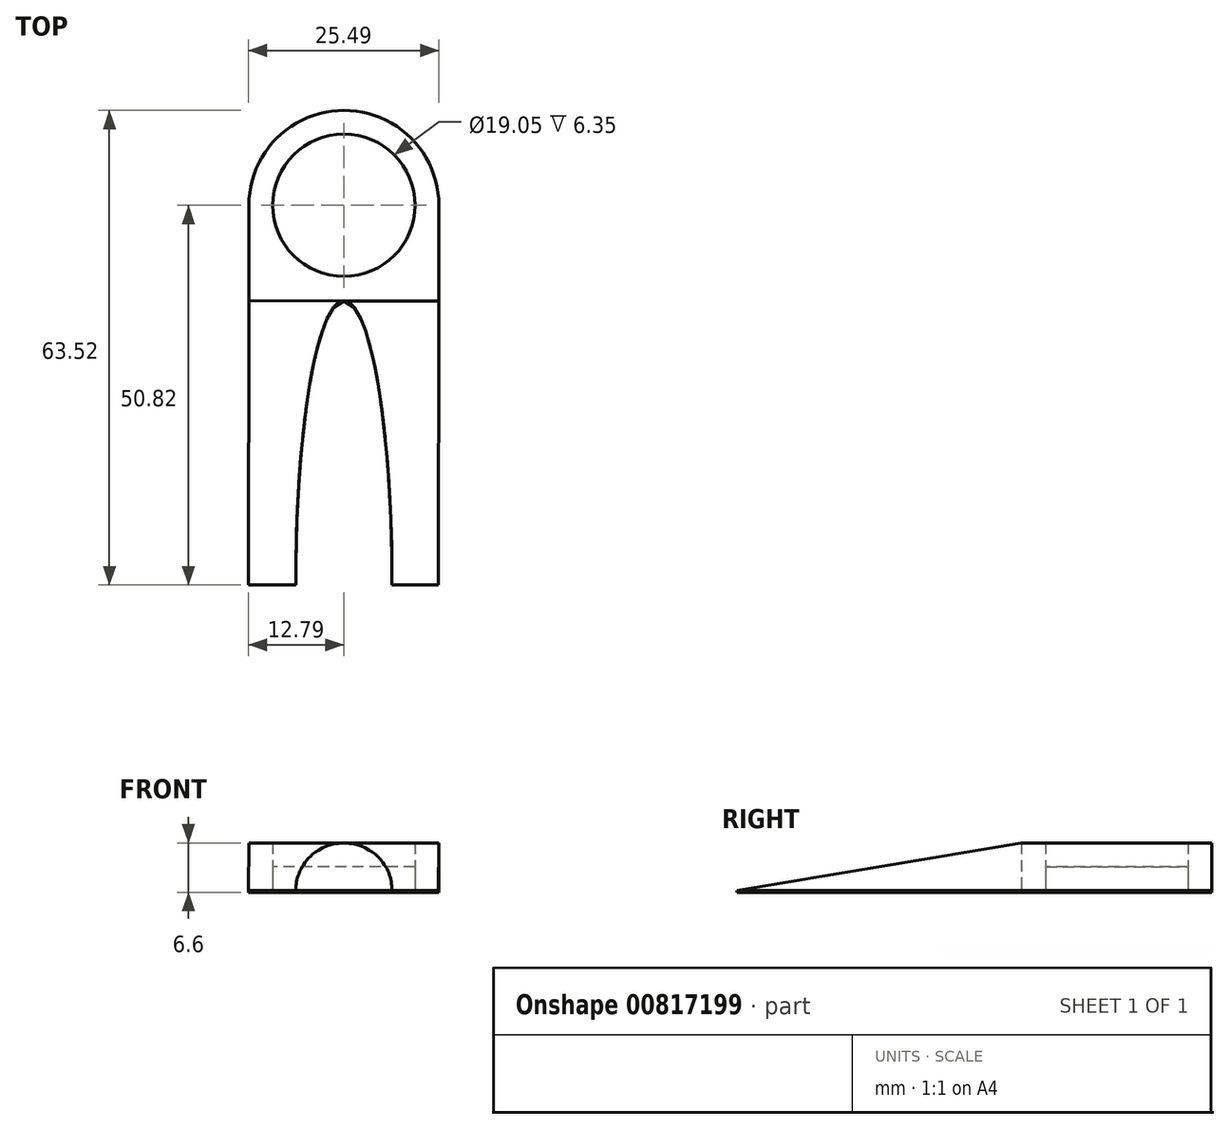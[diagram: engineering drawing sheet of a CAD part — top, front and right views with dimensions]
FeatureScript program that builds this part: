
annotation { "Feature Type Name" : "Feature", "Feature Type Description" : "" }
export const myFeature = defineFeature(function(context is Context, id is Id, definition is map)
    precondition{}
    {
        {
            var Q0;
            Q0=qCreatedBy(makeId("Top.planeOp"),FACE);
            var sketch = newSketch(context, id + "F0", { "sketchPlane" : qUnion([Q0])});
            skArc(sketch, "E0", {"start": v(12.7, -0.02) * mm, "mid": v(0.01, 12.7) * mm, "end": v(-12.7, 0) * mm});
            skLineSegment(sketch, "E1.left", {"start": v(-12.7, 0) * mm, "end": v(-12.79, -50.8) * mm});
            skLineSegment(sketch, "E1.right", {"start": v(12.7, -0.02) * mm, "end": v(12.61, -50.82) * mm});
            skLineSegment(sketch, "E2.0", {"start": v(-12.79, -50.8) * mm, "end": v(-6.44, -50.8) * mm});
            skCircle(sketch, "E3", {"center": v(0, 0) * mm, "radius": 12.7 * mm});
            skPoint(sketch, "E3.second.point", {"position": v(0.01, 12.7) * mm});
            skLineSegment(sketch, "E4.0", {"start": v(-15.96, -50.6) * mm, "end": v(-15.96, -50.82) * mm});
            skLineSegment(sketch, "E5.trimOffspring", {"start": v(15.79, -50.82) * mm, "end": v(15.79, -50.83) * mm});
            skLineSegment(sketch, "E6.trimOffspring", {"start": v(6.26, -50.82) * mm, "end": v(12.61, -50.82) * mm});
            skCircle(sketch, "E7.0", {"center": v(0, 0) * mm, "radius": 9.53 * mm});
            skLineSegment(sketch, "E8", {"start": v(0, 0) * mm, "end": v(0, -12.79) * mm});
            skEllipticalArc(sketch, "E9", {});
            skText(sketch, "E10", { "text": "VD", "fontName": "RobotoSlab-Bold.ttf"});
            skText(sketch, "E11", { "text": "IW", "fontName": "RobotoSlab-Bold.ttf"});
            const initialGuessF0  = {"E9": [0, -0.05069532385659177, 0, 1, 0.03790797373769106, 0.006437097886029921, 4.709195026903625, 1.5736992374698529], "E10": [-0.00655, 0, 1, 0, 0.00692], "E11": [-0.00637, -0.00708, 1, 0, 0.00708]};
            skSetInitialGuess(sketch, initialGuessF0);
            skSolve(sketch);
        }
        {
            var Q0;
            Q0=makeQuery(id+"F0.imprint","IMPRINT",FACE,{"disambiguationData":[TD([[makeQuery(id+"F0.imprint","IMPRINT",EDGE,{"derivedFrom":sQuery(id+"F0.wireOp",EDGE,"E7.0")}),-1.0]])]});
            extrude(context, id + "F1", {"entities" : qUnion([Q0]), "depth" : 6.35 * mm});
        }
        {
            var Q0;
            Q0=makeQuery(id+"F0.imprint","IMPRINT",FACE,{"disambiguationData":[TD([[makeQuery(id+"F0.imprint","IMPRINT",EDGE,{"derivedFrom":sQuery(id+"F0.wireOp",EDGE,"E7.0")}),1.0]])]});
            var Q1;
            Q1=makeQuery(id+"F0.imprint","IMPRINT",FACE,{"disambiguationData":[TD([[makeQuery(id+"F0.imprint","IMPRINT",EDGE,{"derivedFrom":sQuery(id+"F0.wireOp",EDGE,"E10.sketch_text.stroke-0")}),-1.0]])]});
            var Q2;
            Q2=makeQuery(id+"F0.imprint","IMPRINT",FACE,{"disambiguationData":[TD([[makeQuery(id+"F0.imprint","IMPRINT",EDGE,{"derivedFrom":sQuery(id+"F0.wireOp",EDGE,"E10.sketch_text.stroke-18")}),-1.0]])]});
            var Q3;
            Q3=makeQuery(id+"F0.imprint","IMPRINT",FACE,{"disambiguationData":[TD([[makeQuery(id+"F0.imprint","IMPRINT",EDGE,{"derivedFrom":sQuery(id+"F0.wireOp",EDGE,"E11.sketch_text.stroke-0")}),-1.0]])]});
            var Q4;
            {var subQ4=sQuery(id+"F0.wireOp",EDGE,"E11.sketch_text.stroke-19");Q4=makeQuery(id+"F0.imprint","IMPRINT",FACE,{"disambiguationData":[TD([[makeQuery(id+"F0.imprint","IMPRINT",EDGE,{"derivedFrom":subQ4}),-1.0]])]});}
            var Q5;
            Q5=makeQuery(id+"F0.imprint","IMPRINT",FACE,{"disambiguationData":[TD([[makeQuery(id+"F0.imprint","IMPRINT",EDGE,{"derivedFrom":sQuery(id+"F0.wireOp",EDGE,"E11.sketch_text.stroke-12")}),-1.0]])]});
            var Q6;
            Q6=makeQuery(id+"F0.imprint","IMPRINT",FACE,{"disambiguationData":[TD([[makeQuery(id+"F0.imprint","IMPRINT",EDGE,{"derivedFrom":sQuery(id+"F0.wireOp",EDGE,"E10.sketch_text.stroke-31")}),1.0]])]});
            extrude(context, id + "F2", {"entities" : qUnion([Q0, Q1, Q2, Q3, Q4, Q5, Q6]), "depth" : 3.17 * mm});
        }
        {
            var Q0;
            Q0=makeQuery(id+"F0.imprint","IMPRINT",FACE,{"disambiguationData":[TD([[makeQuery(id+"F0.imprint","IMPRINT",EDGE,{"derivedFrom":sQuery(id+"F0.wireOp",EDGE,"E7.0")}),1.0]])]});
            var Q1;
            Q1=makeQuery(id+"F0.imprint","IMPRINT",FACE,{"disambiguationData":[TD([[makeQuery(id+"F0.imprint","IMPRINT",EDGE,{"derivedFrom":sQuery(id+"F0.wireOp",EDGE,"e0804143-4723-42b6-951f-b85cdecca350.sketch_text.stroke-13")}),1.0]])]});
            var Q2;
            Q2=makeQuery(id+"F0.imprint","IMPRINT",FACE,{"disambiguationData":[TD([[makeQuery(id+"F0.imprint","IMPRINT",EDGE,{"derivedFrom":sQuery(id+"F0.wireOp",EDGE,"E10.sketch_text.stroke-18")}),-1.0]])]});
            var Q3;
            Q3=makeQuery(id+"F0.imprint","IMPRINT",FACE,{"disambiguationData":[TD([[makeQuery(id+"F0.imprint","IMPRINT",EDGE,{"derivedFrom":sQuery(id+"F0.wireOp",EDGE,"E10.sketch_text.stroke-31")}),1.0]])]});
            var Q4;
            Q4=makeQuery(id+"F0.imprint","IMPRINT",FACE,{"disambiguationData":[TD([[makeQuery(id+"F0.imprint","IMPRINT",EDGE,{"derivedFrom":sQuery(id+"F0.wireOp",EDGE,"E11.sketch_text.stroke-12")}),-1.0]])]});
            var Q5;
            {var subQ4=sQuery(id+"F0.wireOp",EDGE,"E11.sketch_text.stroke-19");Q5=makeQuery(id+"F0.imprint","IMPRINT",FACE,{"disambiguationData":[TD([[makeQuery(id+"F0.imprint","IMPRINT",EDGE,{"derivedFrom":subQ4}),-1.0]])]});}
            var Q6;
            Q6=makeQuery(id+"F0.imprint","IMPRINT",FACE,{"disambiguationData":[TD([[makeQuery(id+"F0.imprint","IMPRINT",EDGE,{"derivedFrom":sQuery(id+"F0.wireOp",EDGE,"E10.sketch_text.stroke-0")}),-1.0]])]});
            var Q7;
            Q7=makeQuery(id+"F0.imprint","IMPRINT",FACE,{"disambiguationData":[TD([[makeQuery(id+"F0.imprint","IMPRINT",EDGE,{"derivedFrom":sQuery(id+"F0.wireOp",EDGE,"E11.sketch_text.stroke-0")}),-1.0]])]});
            extrude(context, id + "F3", {"entities" : qUnion([Q0, Q1, Q2, Q3, Q4, Q5, Q6, Q7]), "depth" : 3.17 * mm});
        }
        {
            var Q0;
            {var subQ6=sQuery(id+"F0.wireOp",EDGE,"E1.left");Q0=makeQuery(id+"F0.imprint","IMPRINT",FACE,{"disambiguationData":[TD([[makeQuery(id+"F0.imprint","IMPRINT",EDGE,{"derivedFrom":subQ6}),1.0]])]});}
            var Q1;
            {var subQ7=sQuery(id+"F0.wireOp",EDGE,"E1.right");Q1=makeQuery(id+"F0.imprint","IMPRINT",FACE,{"disambiguationData":[TD([[makeQuery(id+"F0.imprint","IMPRINT",EDGE,{"derivedFrom":subQ7}),-1.0]])]});}
            var Q2;
            Q2=makeQuery(id+"F1.opExtrude","SWEPT_BODY",BODY,{"disambiguationData":[OSD([sQuery(id+"F0.wireOp",EDGE,"E3"),sQuery(id+"F0.wireOp",EDGE,"E7.0")])]});
            extrude(context, id + "F4", {"entities" : qUnion([Q0, Q1]), "operationType" : NewBodyOperationType.ADD, "endBoundEntity" : qUnion([Q2]), "depth" : 6.35 * mm});
        }
        {
            var Q0;
            Q0=makeQuery(id+"F4.opExtrude","SWEPT_FACE",FACE,{"disambiguationData":[OSD([sQuery(id+"F0.wireOp",EDGE,"E1.left")])]});
            var sketch = newSketch(context, id + "F5", { "sketchPlane" : qUnion([Q0])});
            skLineSegment(sketch, "E12", {"start": v(12.79, 0) * mm, "end": v(12.79, 6.35) * mm});
            skLineSegment(sketch, "E13", {"start": v(12.79, 6.35) * mm, "end": v(50.82, 6.35) * mm});
            skLineSegment(sketch, "E14", {"start": v(50.82, 6.35) * mm, "end": v(50.82, 0) * mm});
            skLineSegment(sketch, "E15", {"start": v(50.82, 0) * mm, "end": v(12.79, 6.35) * mm});
            skSolve(sketch);
        }
        {
            var Q0;
            Q0=makeQuery(id+"F5.imprint","IMPRINT",FACE,{"disambiguationData":[TD([[makeQuery(id+"F5.imprint","IMPRINT",EDGE,{"derivedFrom":sQuery(id+"F5.wireOp",EDGE,"E13")}),-1.0]])]});
            extrude(context, id + "F6", {"entities" : qUnion([Q0]), "operationType" : NewBodyOperationType.REMOVE, "endBound" : BoundingType.THROUGH_ALL, "oppositeDirection" : true, "depth" : 25.4 * mm});
        }
        {
            var Q0;
            {var subQ6=sQuery(id+"F0.wireOp",EDGE,"E1.left");Q0=makeQuery(id+"F0.imprint","IMPRINT",FACE,{"disambiguationData":[TD([[makeQuery(id+"F0.imprint","IMPRINT",EDGE,{"derivedFrom":subQ6}),1.0]])]});}
            var Q1;
            {var subQ7=sQuery(id+"F0.wireOp",EDGE,"E1.right");Q1=makeQuery(id+"F0.imprint","IMPRINT",FACE,{"disambiguationData":[TD([[makeQuery(id+"F0.imprint","IMPRINT",EDGE,{"derivedFrom":subQ7}),-1.0]])]});}
            var Q2;
            Q2=makeQuery(id+"F0.imprint","IMPRINT",FACE,{"disambiguationData":[TD([[makeQuery(id+"F0.imprint","IMPRINT",EDGE,{"derivedFrom":sQuery(id+"F0.wireOp",EDGE,"E7.0")}),-1.0]])]});
            var Q3;
            Q3=makeQuery(id+"F0.imprint","IMPRINT",FACE,{"disambiguationData":[TD([[makeQuery(id+"F0.imprint","IMPRINT",EDGE,{"derivedFrom":sQuery(id+"F0.wireOp",EDGE,"E7.0")}),1.0]])]});
            var Q4;
            Q4=makeQuery(id+"F0.imprint","IMPRINT",FACE,{"disambiguationData":[TD([[makeQuery(id+"F0.imprint","IMPRINT",EDGE,{"derivedFrom":sQuery(id+"F0.wireOp",EDGE,"E11.sketch_text.stroke-0")}),-1.0]])]});
            var Q5;
            {var subQ4=sQuery(id+"F0.wireOp",EDGE,"E11.sketch_text.stroke-19");Q5=makeQuery(id+"F0.imprint","IMPRINT",FACE,{"disambiguationData":[TD([[makeQuery(id+"F0.imprint","IMPRINT",EDGE,{"derivedFrom":subQ4}),-1.0]])]});}
            var Q6;
            Q6=makeQuery(id+"F0.imprint","IMPRINT",FACE,{"disambiguationData":[TD([[makeQuery(id+"F0.imprint","IMPRINT",EDGE,{"derivedFrom":sQuery(id+"F0.wireOp",EDGE,"E11.sketch_text.stroke-12")}),-1.0]])]});
            var Q7;
            Q7=makeQuery(id+"F0.imprint","IMPRINT",FACE,{"disambiguationData":[TD([[makeQuery(id+"F0.imprint","IMPRINT",EDGE,{"derivedFrom":sQuery(id+"F0.wireOp",EDGE,"E10.sketch_text.stroke-0")}),-1.0]])]});
            var Q8;
            Q8=makeQuery(id+"F0.imprint","IMPRINT",FACE,{"disambiguationData":[TD([[makeQuery(id+"F0.imprint","IMPRINT",EDGE,{"derivedFrom":sQuery(id+"F0.wireOp",EDGE,"E10.sketch_text.stroke-18")}),-1.0]])]});
            var Q9;
            Q9=makeQuery(id+"F0.imprint","IMPRINT",FACE,{"disambiguationData":[TD([[makeQuery(id+"F0.imprint","IMPRINT",EDGE,{"derivedFrom":sQuery(id+"F0.wireOp",EDGE,"E10.sketch_text.stroke-31")}),1.0]])]});
            extrude(context, id + "F7", {"entities" : qUnion([Q0, Q1, Q2, Q3, Q4, Q5, Q6, Q7, Q8, Q9]), "oppositeDirection" : true, "depth" : 0.25 * mm});
        }
    });
